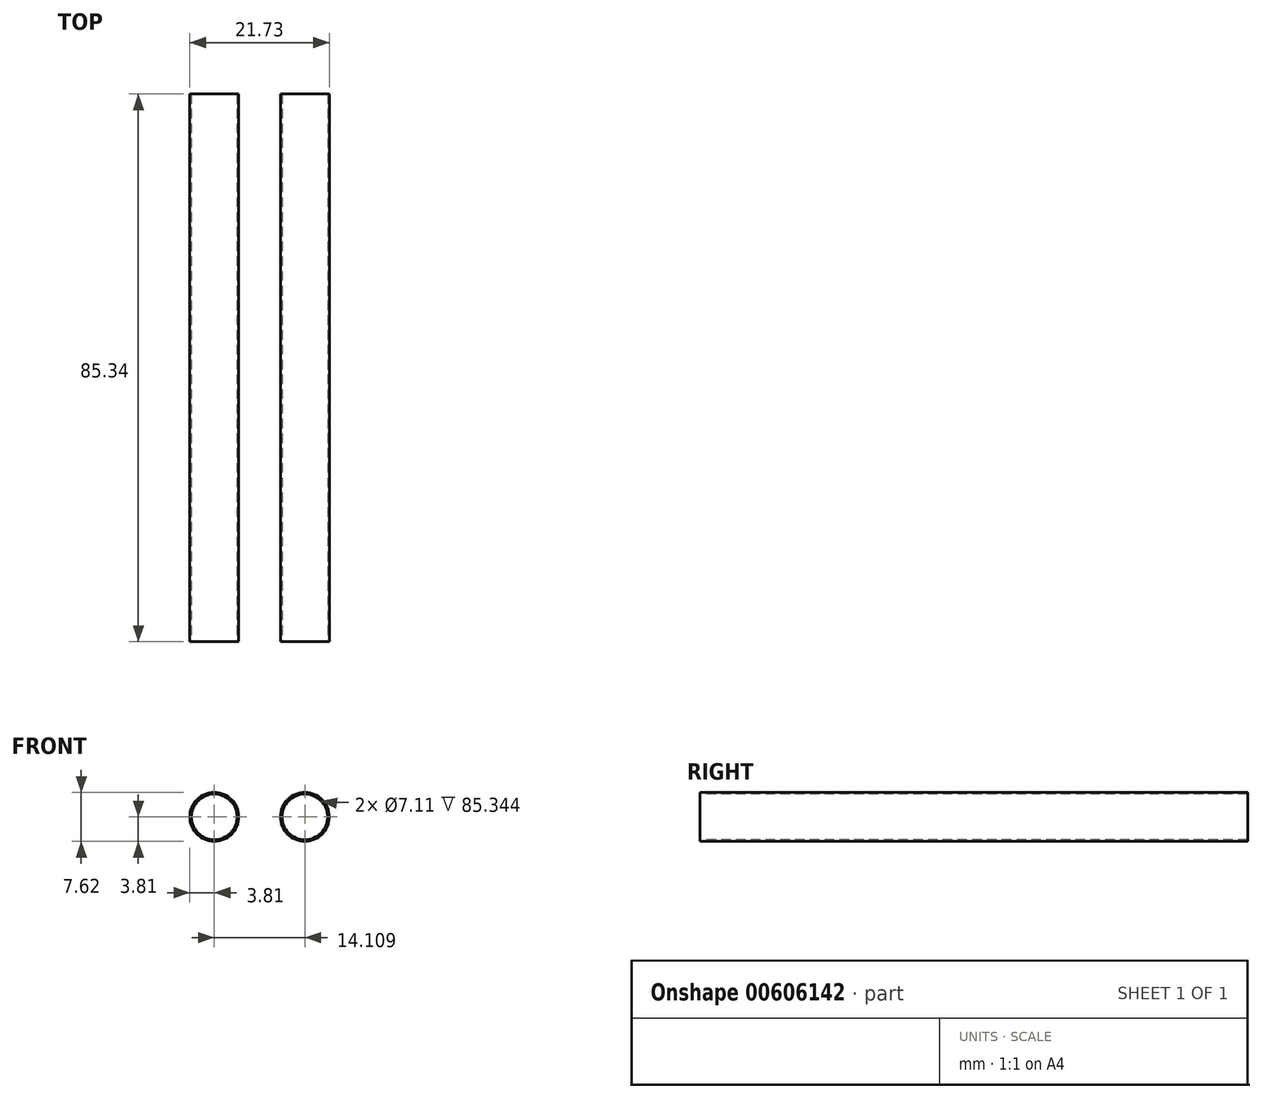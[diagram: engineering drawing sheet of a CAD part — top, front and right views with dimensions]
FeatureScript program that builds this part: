
annotation { "Feature Type Name" : "Feature", "Feature Type Description" : "" }
export const myFeature = defineFeature(function(context is Context, id is Id, definition is map)
    precondition{}
    {
        {
            var Q0;
            Q0=qCreatedBy(makeId("Front.planeOp"),FACE);
            var sketch = newSketch(context, id + "F0", { "sketchPlane" : qUnion([Q0])});
            skCircle(sketch, "E0", {"center": v(0, 0) * mm, "radius": 3.81 * mm});
            skSolve(sketch);
        }
        {
            var Q0;
            Q0=qCreatedBy(makeId("Front.planeOp"),FACE);
            var sketch = newSketch(context, id + "F1", { "sketchPlane" : qUnion([Q0])});
            skCircle(sketch, "E1", {"center": v(14.1, 0) * mm, "radius": 3.81 * mm});
            skSolve(sketch);
        }
        {
            var Q0;
            Q0=makeQuery(id+"F0.imprint","IMPRINT",FACE,{"disambiguationData":[TD([[makeQuery(id+"F0.imprint","IMPRINT",EDGE,{"derivedFrom":sQuery(id+"F0.wireOp",EDGE,"E0")}),1.0]])]});
            var Q1;
            Q1=makeQuery(id+"F1.imprint","IMPRINT",FACE,{"disambiguationData":[TD([[makeQuery(id+"F1.imprint","IMPRINT",EDGE,{"derivedFrom":sQuery(id+"F1.wireOp",EDGE,"E1")}),1.0]])]});
            extrude(context, id + "F2", {"entities" : qUnion([Q0, Q1]), "depth" : 85.34 * mm, "offsetDistance" : 25.4 * mm});
        }
        {
            var Q0;
            Q0=makeQuery(id+"F2.opExtrude","CAP_FACE",FACE,{"disambiguationData":[OSD([sQuery(id+"F1.wireOp",EDGE,"E1")])],"isStart":false});
            var sketch = newSketch(context, id + "F3", { "sketchPlane" : qUnion([Q0])});
            skCircle(sketch, "E2", {"center": v(14.1, 0) * mm, "radius": 3.56 * mm});
            skSolve(sketch);
        }
        {
            var Q0;
            Q0=makeQuery(id+"F2.opExtrude","CAP_FACE",FACE,{"disambiguationData":[OSD([sQuery(id+"F0.wireOp",EDGE,"E0")])],"isStart":false});
            var sketch = newSketch(context, id + "F4", { "sketchPlane" : qUnion([Q0])});
            skCircle(sketch, "E3", {"center": v(0, 0) * mm, "radius": 3.56 * mm});
            skSolve(sketch);
        }
        {
            var Q0;
            Q0=makeQuery(id+"F4.imprint","IMPRINT",FACE,{"disambiguationData":[TD([[makeQuery(id+"F4.imprint","IMPRINT",EDGE,{"derivedFrom":sQuery(id+"F4.wireOp",EDGE,"E3")}),1.0]])]});
            extrude(context, id + "F5", {"entities" : qUnion([Q0]), "operationType" : NewBodyOperationType.REMOVE, "oppositeDirection" : true, "depth" : 101.1 * mm, "offsetDistance" : 25.4 * mm});
        }
        {
            var Q0;
            Q0=makeQuery(id+"F3.imprint","IMPRINT",FACE,{"disambiguationData":[TD([[makeQuery(id+"F3.imprint","IMPRINT",EDGE,{"derivedFrom":sQuery(id+"F3.wireOp",EDGE,"E2")}),1.0]])]});
            extrude(context, id + "F6", {"entities" : qUnion([Q0]), "operationType" : NewBodyOperationType.REMOVE, "oppositeDirection" : true, "depth" : 100.33 * mm, "offsetDistance" : 25.4 * mm});
        }
    });
